# Revit family: Curtain_Wall_Door-Automatic_Swing-Nabco-Sideload_Header-Outswing-ADA
name_source: partatom
category: Doors
revit_build: Autodesk Revit 2015 (Build: 20140223_1515(x64)
units: mm (PartAtom-declared; Revit-internal decimal feet)

## types (4) — shared parameters
Date Last Modified = March 9, 2012
Equipment Abbreviation = ASD
Family Version = 1.0.0
Function = Exterior
Is Void = Yes
Manufacturer = NABCO Entrances Inc.
Model = See Part Number
Model Disclaimer = This model represents a highly customizable product.  Contact NABCO Entrances Inc. for more information
Model ID = 3A81A627-429F-4D73-801C-BF140E3A4C78
Product Documentation Link = http://www.nabcoentrances.com
Provide Feedback = https://www.surveymonkey.com
Thickness = 1.75 "
URL = http://www.nabcoentrances.com

## per-type parameters (varying)
| type | Description | Part Description | z Type |
| Narrow Stile, Hydraulic Closer | Automatic Swing, Sideload Header, Hydraulic Closer, Outswing, Narrow Stile | Automatic Swing, Sideload Header, Hydraulic Closer, Outswing, Narrow Stile | 3 |
| Medium Stile, Hydraulic Closer | Automatic Swing, Sideload Header, Hydraulic Closer, Outswing, Medium Stile | Automatic Swing, Sideload Header, Hydraulic Closer, Outswing, Medium Stile | 1 |
| Medium Stile, Spring Closer | Automatic Swing, Sideload Header, Spring Closer, Outswing, Medium Stile | Automatic Swing, Sideload Header, Spring Closer, Outswing, Medium Stile | 2 |
| Narrow Stile, Spring Closer | Automatic Swing, Sideload Header, Spring Closer, Outswing, Narrow Stile | Automatic Swing, Sideload Header, Spring Closer, Outswing, Narrow Stile | 4 |

## geometry (parser evidence)
native form markers: Blend x4, Sweep x2
no freeform markers — native parametric forms only
